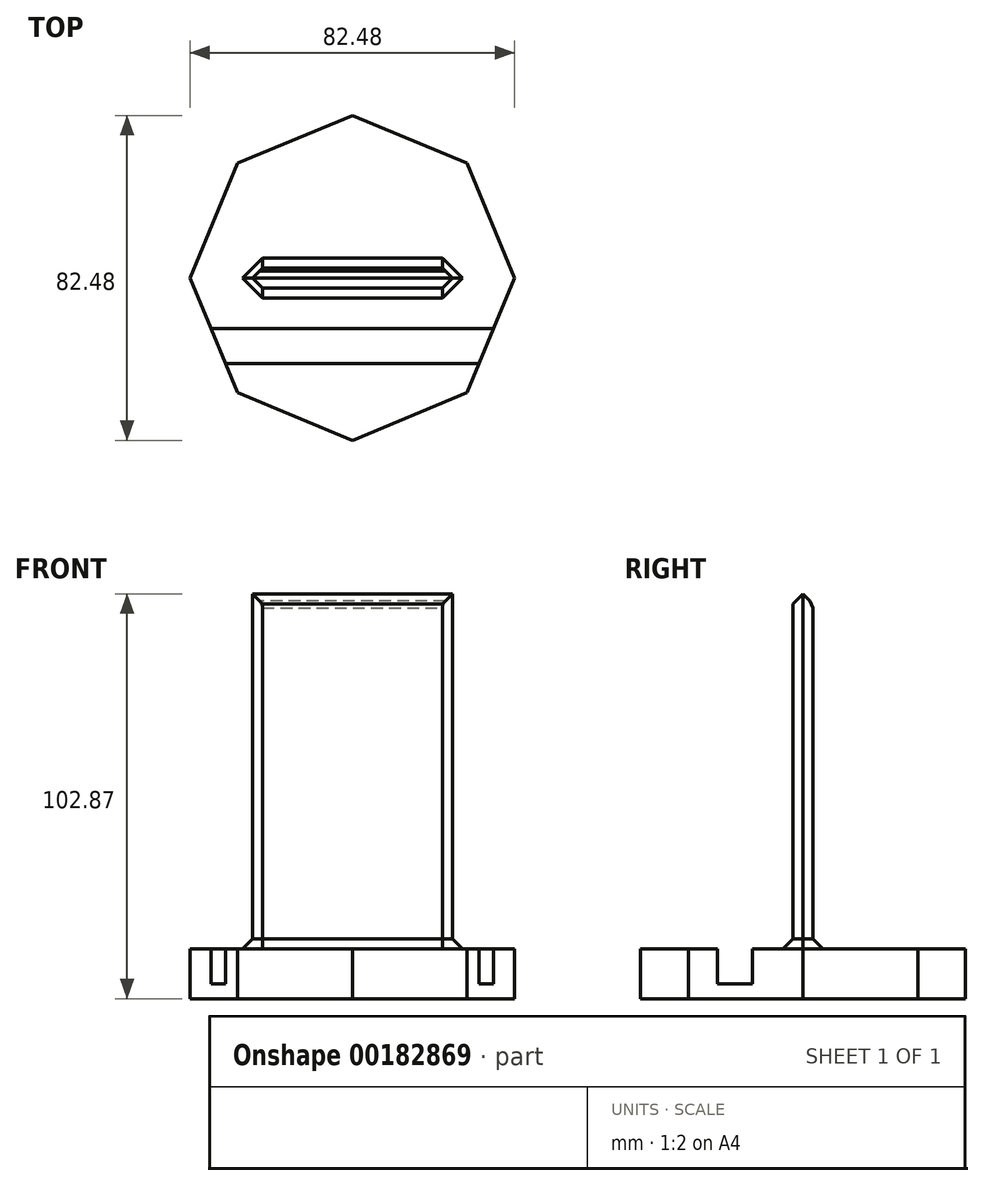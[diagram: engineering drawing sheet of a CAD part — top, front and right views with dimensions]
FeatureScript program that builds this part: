
annotation { "Feature Type Name" : "Feature", "Feature Type Description" : "" }
export const myFeature = defineFeature(function(context is Context, id is Id, definition is map)
    precondition{}
    {
        {
            var Q0;
            Q0=qCreatedBy(makeId("Top.planeOp"),FACE);
            var sketch = newSketch(context, id + "F0", { "sketchPlane" : qUnion([Q0])});
            skCircle(sketch, "E0.cCircle", {"center": v(0, 0) * mm, "radius": 38.1 * mm, "construction": true});
            skLineSegment(sketch, "E0.0", {"start": v(0, 41.24) * mm, "end": v(29.16, 29.16) * mm});
            skLineSegment(sketch, "E0.1", {"start": v(29.16, 29.16) * mm, "end": v(41.24, 0) * mm});
            skLineSegment(sketch, "E0.2", {"start": v(41.24, 0) * mm, "end": v(29.16, -29.16) * mm});
            skLineSegment(sketch, "E0.3", {"start": v(29.16, -29.16) * mm, "end": v(0, -41.24) * mm});
            skLineSegment(sketch, "E0.4", {"start": v(0, -41.24) * mm, "end": v(-29.16, -29.16) * mm});
            skLineSegment(sketch, "E0.5", {"start": v(-29.16, -29.16) * mm, "end": v(-41.24, 0) * mm});
            skLineSegment(sketch, "E0.6", {"start": v(-41.24, 0) * mm, "end": v(-29.16, 29.16) * mm});
            skLineSegment(sketch, "E0.7", {"start": v(-29.16, 29.16) * mm, "end": v(0, 41.24) * mm});
            skPoint(sketch, "E0.0.midPoint", {"position": v(14.58, 35.2) * mm});
            skSolve(sketch);
        }
        {
            var Q0;
            Q0 = qSketchRegion(id + "F0", true);
            extrude(context, id + "F1", {"entities" : qUnion([Q0]), "depth" : 8.9 * mm, "hasSecondDirection" : true, "secondDirectionOppositeDirection" : true, "secondDirectionDepth" : 3.8 * mm});
        }
        {
            var Q0;
            Q0=qCreatedBy(makeId("Top.planeOp"),FACE);
            var sketch = newSketch(context, id + "F2", { "sketchPlane" : qUnion([Q0])});
            skLineSegment(sketch, "E1.bottom", {"start": v(63.5, -12.9) * mm, "end": v(-63.5, -12.9) * mm});
            skLineSegment(sketch, "E1.top", {"start": v(63.5, -21.8) * mm, "end": v(-63.5, -21.8) * mm});
            skLineSegment(sketch, "E1.left", {"start": v(63.5, -12.9) * mm, "end": v(63.5, -21.8) * mm});
            skLineSegment(sketch, "E1.right", {"start": v(-63.5, -12.9) * mm, "end": v(-63.5, -21.8) * mm});
            skPoint(sketch, "E1.middle", {"position": v(0, -17.35) * mm});
            skSolve(sketch);
        }
        {
            var Q0;
            Q0 = qSketchRegion(id + "F2", true);
            extrude(context, id + "F3", {"entities" : qUnion([Q0]), "operationType" : NewBodyOperationType.REMOVE, "depth" : 25.4 * mm});
        }
        {
            var Q0;
            Q0=qCreatedBy(makeId("Top.planeOp"),FACE);
            var sketch = newSketch(context, id + "F4", { "sketchPlane" : qUnion([Q0])});
            skLineSegment(sketch, "E2.bottom", {"start": v(25.4, 2.54) * mm, "end": v(-25.4, 2.54) * mm});
            skLineSegment(sketch, "E2.top", {"start": v(25.4, -2.54) * mm, "end": v(-25.4, -2.54) * mm});
            skLineSegment(sketch, "E2.left", {"start": v(25.4, 2.54) * mm, "end": v(25.4, -2.54) * mm});
            skLineSegment(sketch, "E2.right", {"start": v(-25.4, 2.54) * mm, "end": v(-25.4, -2.54) * mm});
            skPoint(sketch, "E2.middle", {"position": v(0, 0) * mm});
            skSolve(sketch);
        }
        {
            var Q0;
            Q0 = qSketchRegion(id + "F4", true);
            extrude(context, id + "F5", {"entities" : qUnion([Q0]), "operationType" : NewBodyOperationType.ADD, "depth" : 101.6 * mm});
        }
        {
            var Q0;
            Q0=makeQuery(id+"F5.opExtrude","CAP_EDGE",EDGE,{"disambiguationData":[OSD([sQuery(id+"F4.wireOp",EDGE,"E2.top")])],"isStart":false});
            var Q1;
            Q1=makeQuery(id+"F5.opExtrude","CAP_EDGE",EDGE,{"disambiguationData":[OSD([sQuery(id+"F4.wireOp",EDGE,"E2.bottom")])],"isStart":false});
            chamfer(context, id + "F6", {"entities" : qUnion([Q0, Q1]), "width" : 5.08 * mm, "tangentPropagation" : true});
        }
        {
            var Q0;
            Q0=makeQuery(id+"F5.opExtrude","SWEPT_FACE",FACE,{"disambiguationData":[OSD([sQuery(id+"F4.wireOp",EDGE,"E2.bottom")])]});
            var Q1;
            {var subQ0=sQuery(id+"F0.wireOp",EDGE,"E0.5");var subQ1=sQuery(id+"F0.wireOp",EDGE,"E0.2");var subQ2=sQuery(id+"F0.wireOp",EDGE,"E0.1");var subQ3=sQuery(id+"F0.wireOp",EDGE,"E0.0");var subQ4=sQuery(id+"F0.wireOp",EDGE,"E0.6");var subQ5=sQuery(id+"F0.wireOp",EDGE,"E0.7");Q1=makeQuery(id+"F5.boolean.opBoolean","INTERSECT",EDGE,{"derivedFrom":[makeQuery(id+"F3.boolean.opBoolean","SPLIT",FACE,{"disambiguationData":[TD([makeQuery(id+"F1.opExtrude","SWEPT_FACE",FACE,{"disambiguationData":[OSD([subQ3])]})])],"derivedFrom":makeQuery(id+"F1.opExtrude","CAP_FACE",FACE,{"disambiguationData":[OSD([subQ3,subQ2,subQ1,sQuery(id+"F0.wireOp",EDGE,"E0.3"),sQuery(id+"F0.wireOp",EDGE,"E0.4"),subQ0,subQ4,subQ5])],"isStart":false})}),makeQuery(id+"F5.opExtrude","SWEPT_FACE",FACE,{"disambiguationData":[OSD([sQuery(id+"F4.wireOp",EDGE,"E2.top")])]})]});}
            var Q2;
            Q2=makeQuery(id+"F5.opExtrude","SWEPT_EDGE",EDGE,{"disambiguationData":[OSD([sQuery(id+"F4.wireOp",EDGE,"E2.top"),sQuery(id+"F4.wireOp",EDGE,"E2.left")])]});
            var Q3;
            Q3=makeQuery(id+"F5.opExtrude","SWEPT_EDGE",EDGE,{"disambiguationData":[OSD([sQuery(id+"F4.wireOp",EDGE,"E2.top"),sQuery(id+"F4.wireOp",EDGE,"E2.right")])]});
            chamfer(context, id + "F7", {"entities" : qUnion([Q0, Q1, Q2, Q3]), "width" : 2.54 * mm, "tangentPropagation" : true});
        }
    });
